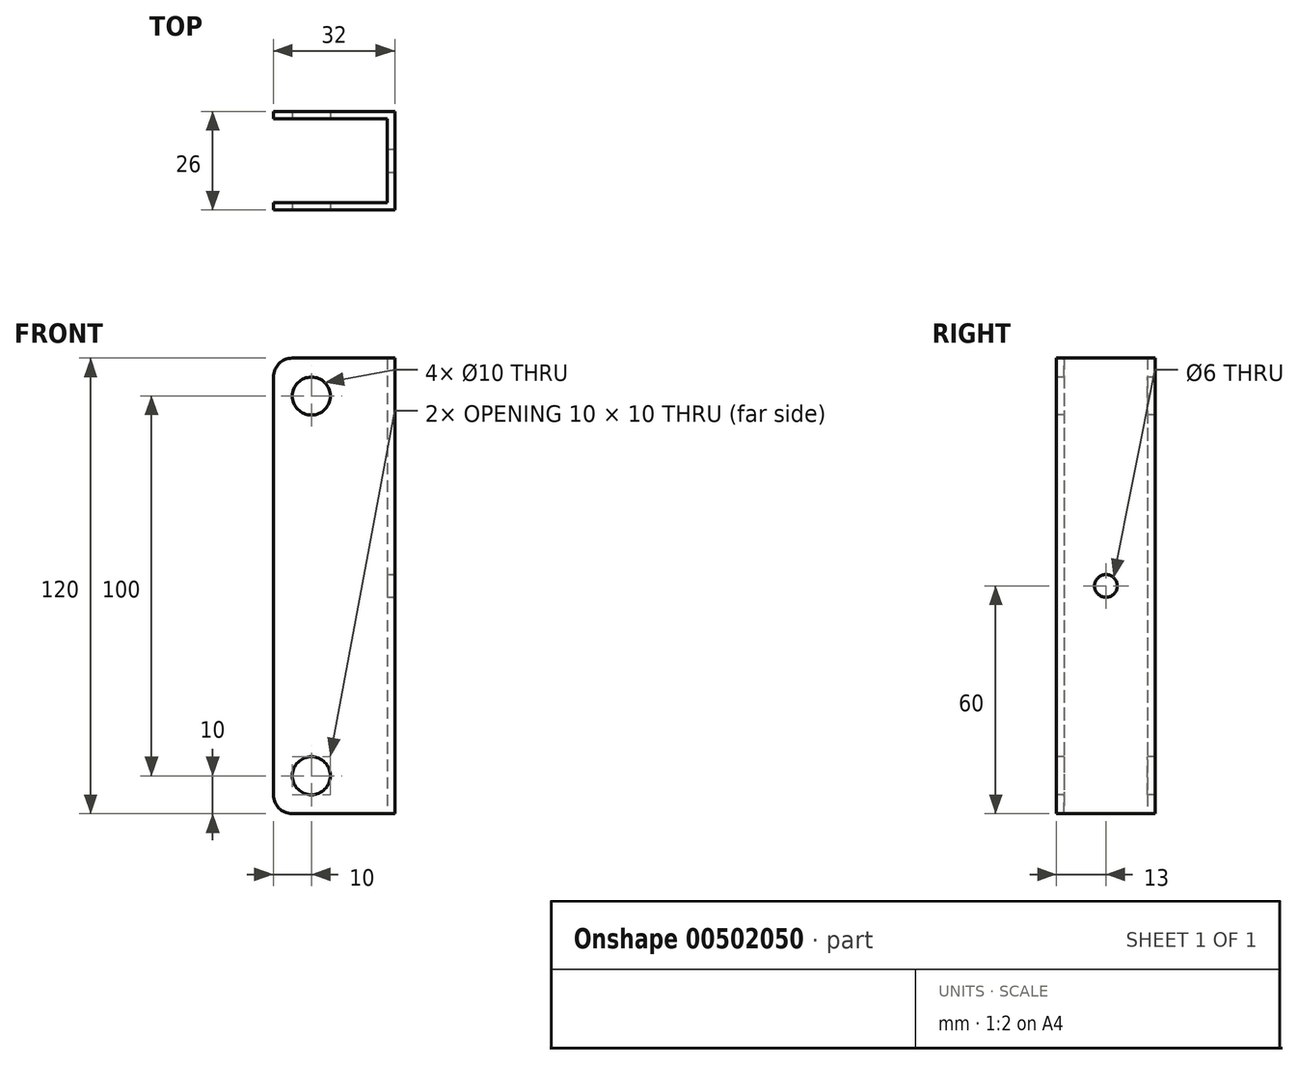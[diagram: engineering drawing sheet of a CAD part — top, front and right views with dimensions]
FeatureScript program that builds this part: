
annotation { "Feature Type Name" : "Feature", "Feature Type Description" : "" }
export const myFeature = defineFeature(function(context is Context, id is Id, definition is map)
    precondition{}
    {
        {
            var Q0;
            Q0=qCreatedBy(makeId("Top.planeOp"),FACE);
            var sketch = newSketch(context, id + "F0", { "sketchPlane" : qUnion([Q0])});
            skLineSegment(sketch, "E0", {"start": v(0, 0) * mm, "end": v(30, 0) * mm});
            skLineSegment(sketch, "E1", {"start": v(30, 0) * mm, "end": v(30, 22) * mm});
            skLineSegment(sketch, "E2", {"start": v(30, 22) * mm, "end": v(0, 22) * mm});
            skLineSegment(sketch, "E3", {"start": v(0, 22) * mm, "end": v(0, 24) * mm});
            skLineSegment(sketch, "E4", {"start": v(0, 24) * mm, "end": v(32, 24) * mm});
            skLineSegment(sketch, "E5", {"start": v(32, 24) * mm, "end": v(32, -2) * mm});
            skLineSegment(sketch, "E6", {"start": v(32, -2) * mm, "end": v(0, -2) * mm});
            skLineSegment(sketch, "E7", {"start": v(0, -2) * mm, "end": v(0, 0) * mm});
            skSolve(sketch);
        }
        {
            var Q0;
            Q0=makeQuery(id+"F0.imprint","IMPRINT",FACE,{"disambiguationData":[TD([[makeQuery(id+"F0.imprint","IMPRINT",EDGE,{"derivedFrom":sQuery(id+"F0.wireOp",EDGE,"E0")}),-1.0]])]});
            extrude(context, id + "F1", {"entities" : qUnion([Q0]), "depth" : 120 * mm});
        }
        {
            var Q0;
            Q0=makeQuery(id+"F1.opExtrude","SWEPT_FACE",FACE,{"disambiguationData":[OSD([sQuery(id+"F0.wireOp",EDGE,"E6")])]});
            var sketch = newSketch(context, id + "F2", { "sketchPlane" : qUnion([Q0])});
            skLineSegment(sketch, "E8", {"start": v(0, 120) * mm, "end": v(10, 120) * mm});
            skLineSegment(sketch, "E9", {"start": v(10, 120) * mm, "end": v(10, 110) * mm});
            skLineSegment(sketch, "E10", {"start": v(10, 110) * mm, "end": v(10, 10) * mm});
            skSolve(sketch);
        }
        {
            var Q0;
            Q0=sQuery(id+"F2.wireOp",VERTEX,"E10.start");
            var Q1;
            Q1=sQuery(id+"F2.wireOp",VERTEX,"E10.end");
            var Q2;
            Q2=makeQuery(id+"F1.opExtrude","SWEPT_BODY",BODY,{"disambiguationData":[OSD([sQuery(id+"F0.wireOp",EDGE,"E0"),sQuery(id+"F0.wireOp",EDGE,"E1"),sQuery(id+"F0.wireOp",EDGE,"E2"),sQuery(id+"F0.wireOp",EDGE,"E3"),sQuery(id+"F0.wireOp",EDGE,"E4"),sQuery(id+"F0.wireOp",EDGE,"E5"),sQuery(id+"F0.wireOp",EDGE,"E6"),sQuery(id+"F0.wireOp",EDGE,"E7")])]});
            hole(context, id + "F3", {"style" : HoleStyle.SIMPLE, "endStyle" : HoleEndStyle.THROUGH, "holeDiameter" : 10 * mm, "isTappedThrough" : true, "tappedDepth" : 12 * mm, "tapClearance" : 3, "locations" : qUnion([Q0, Q1]), "scope" : qUnion([Q2])});
        }
        {
            var Q0;
            Q0=makeQuery(id+"F1.opExtrude","SWEPT_FACE",FACE,{"disambiguationData":[OSD([sQuery(id+"F0.wireOp",EDGE,"E5")])]});
            var sketch = newSketch(context, id + "F4", { "sketchPlane" : qUnion([Q0])});
            skLineSegment(sketch, "E11", {"start": v(11, 120) * mm, "end": v(11, 60) * mm});
            skPoint(sketch, "E11.endSnap0", {"position": v(24, 60) * mm});
            skSolve(sketch);
        }
        {
            var Q0;
            Q0=sQuery(id+"F4.wireOp",VERTEX,"E11.end");
            var Q1;
            Q1=makeQuery(id+"F1.opExtrude","SWEPT_BODY",BODY,{"disambiguationData":[OSD([sQuery(id+"F0.wireOp",EDGE,"E0"),sQuery(id+"F0.wireOp",EDGE,"E1"),sQuery(id+"F0.wireOp",EDGE,"E2"),sQuery(id+"F0.wireOp",EDGE,"E3"),sQuery(id+"F0.wireOp",EDGE,"E4"),sQuery(id+"F0.wireOp",EDGE,"E5"),sQuery(id+"F0.wireOp",EDGE,"E6"),sQuery(id+"F0.wireOp",EDGE,"E7")])]});
            hole(context, id + "F5", {"style" : HoleStyle.SIMPLE, "endStyle" : HoleEndStyle.THROUGH, "holeDiameter" : 6 * mm, "isTappedThrough" : true, "tappedDepth" : 12 * mm, "tapClearance" : 3, "locations" : qUnion([Q0]), "scope" : qUnion([Q1])});
        }
        {
            var Q0;
            Q0=makeQuery(id+"F1.opExtrude","CAP_EDGE",EDGE,{"disambiguationData":[OSD([sQuery(id+"F0.wireOp",EDGE,"E7")])],"isStart":false});
            var Q1;
            Q1=makeQuery(id+"F1.opExtrude","CAP_EDGE",EDGE,{"disambiguationData":[OSD([sQuery(id+"F0.wireOp",EDGE,"E3")])],"isStart":false});
            var Q2;
            Q2=makeQuery(id+"F1.opExtrude","CAP_EDGE",EDGE,{"disambiguationData":[OSD([sQuery(id+"F0.wireOp",EDGE,"E3")])],"isStart":true});
            var Q3;
            Q3=makeQuery(id+"F1.opExtrude","CAP_EDGE",EDGE,{"disambiguationData":[OSD([sQuery(id+"F0.wireOp",EDGE,"E7")])],"isStart":true});
            fillet(context, id + "F6", {"entities" : qUnion([Q0, Q1, Q2, Q3]), "radius" : 5 * mm, "tangentPropagation" : true, "allowEdgeOverflow" : false});
        }
    });
